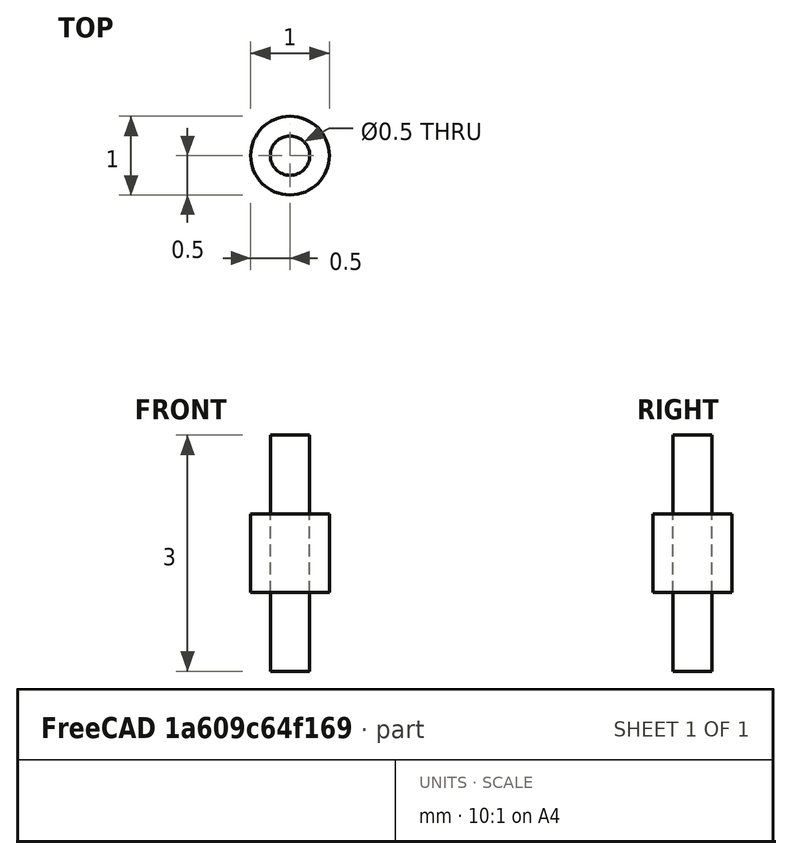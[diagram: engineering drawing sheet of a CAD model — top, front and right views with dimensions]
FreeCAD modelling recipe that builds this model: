
FCSTD DOCUMENT  (FreeCAD 0.19R24291 (Git))
Label: coil_pins01
License: All rights reserved
LicenseURL: http://en.wikipedia.org/wiki/All_rights_reserved
objects: Spreadsheet::Sheet×1, PartDesign::Body×1, Part::FeaturePython×1, Part::Cylinder×1
note: 3 computed .brp shape members not serialized (recipe doc carries the construction recipe); baked Part::Feature solids carry a one-line shape summary decoded from their .brp

FEATURE [Spreadsheet::Sheet] Spreadsheet
  cells = A2=coil pins; B2=rad; C2(pin_r)=0.5; D2(pin_wr)=0.25; B3=rad ins; C3(pin_ri)=0.25; B4=ln; C4(pin_ln)=1; D4(pin_wln)=3
FEATURE [PartDesign::Body] Body
  Origin = -> Origin
FEATURE [Part::FeaturePython] Tube  # WARN: FeaturePython — macro-defined, semantics opaque (R4)
  AttacherType = Attacher::AttachEngine3D
  Height = 1
  InnerRadius = 0.25
  OuterRadius = 0.5
  expr: OuterRadius = Spreadsheet.pin_r
  expr: InnerRadius = Spreadsheet.pin_ri
  expr: Height = Spreadsheet.pin_ln
FEATURE [Part::Cylinder] Cylinder
  Angle = 360
  AttacherType = Attacher::AttachEngine3D
  Height = 3
  Placement = pos=(0,0,-1) rot=(0,0,1;0rad)
  Radius = 0.25
  expr: Radius = Spreadsheet.pin_wr
  expr: Height = Spreadsheet.pin_wln
